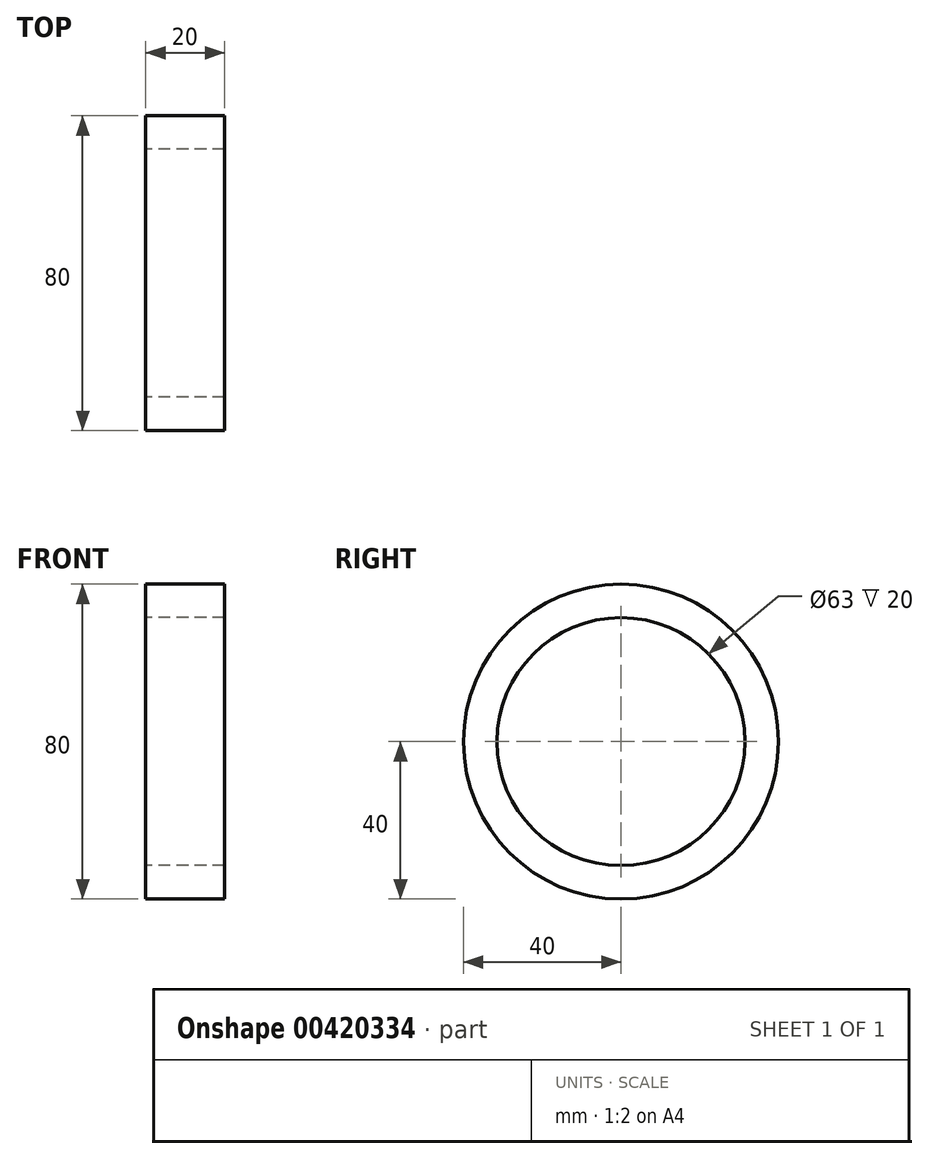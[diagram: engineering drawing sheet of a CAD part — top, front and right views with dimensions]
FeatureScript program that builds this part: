
annotation { "Feature Type Name" : "Feature", "Feature Type Description" : "" }
export const myFeature = defineFeature(function(context is Context, id is Id, definition is map)
    precondition{}
    {
        {
            var Q0;
            Q0=qCreatedBy(makeId("Right.planeOp"),FACE);
            var sketch = newSketch(context, id + "F0", { "sketchPlane" : qUnion([Q0])});
            skCircle(sketch, "E0", {"center": v(0, 0) * mm, "radius": 31.5 * mm});
            skCircle(sketch, "E1", {"center": v(0, 0) * mm, "radius": 40 * mm});
            skSolve(sketch);
        }
        {
            var Q0;
            Q0=qSketchRegion(id+"F0",true);
            extrude(context, id + "F1", {"entities" : qUnion([Q0]), "depth" : 20 * mm});
        }
    });
